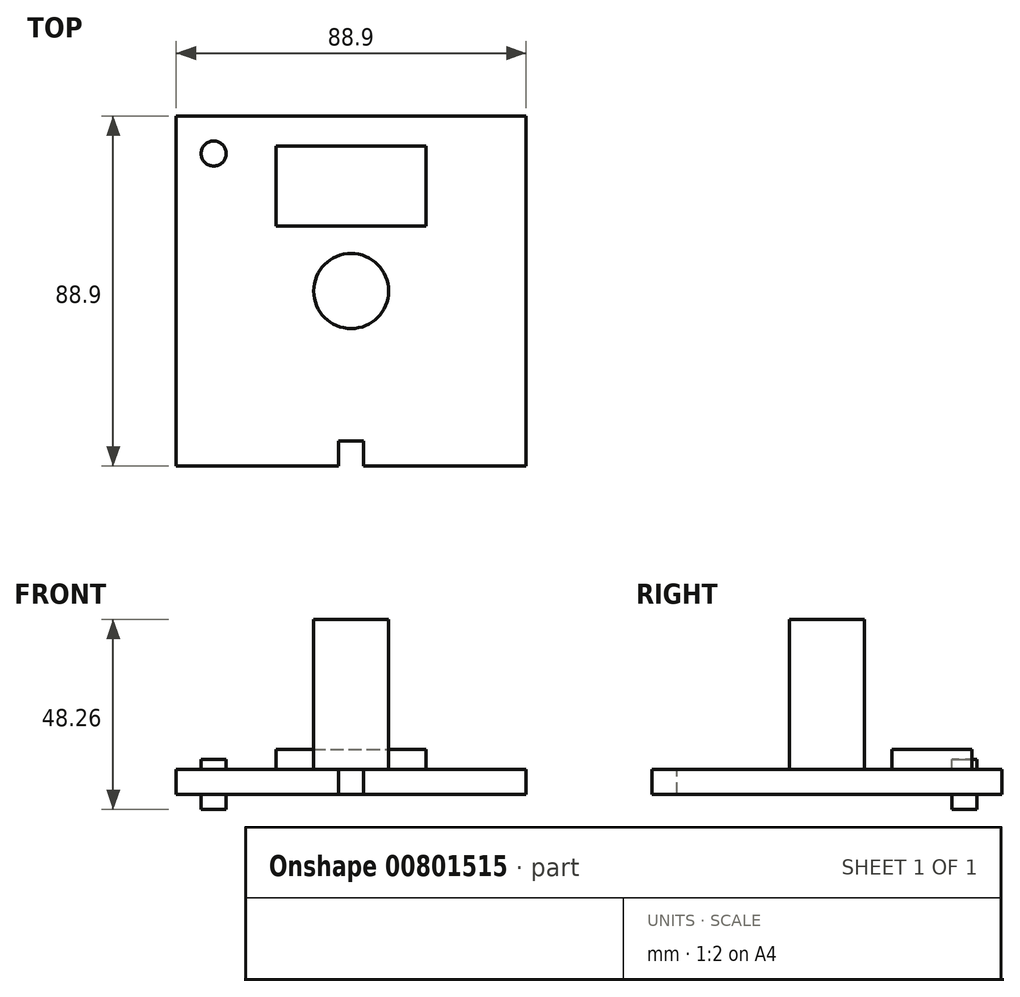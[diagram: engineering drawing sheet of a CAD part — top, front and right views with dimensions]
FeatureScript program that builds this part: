
annotation { "Feature Type Name" : "Feature", "Feature Type Description" : "" }
export const myFeature = defineFeature(function(context is Context, id is Id, definition is map)
    precondition{}
    {
        {
            var Q0;
            Q0=qCreatedBy(makeId("Top.planeOp"),FACE);
            var sketch = newSketch(context, id + "F0", { "sketchPlane" : qUnion([Q0])});
            skLineSegment(sketch, "E0.bottom", {"start": v(-44.45, 44.45) * mm, "end": v(44.45, 44.45) * mm});
            skLineSegment(sketch, "E0.top", {"start": v(-44.45, -44.45) * mm, "end": v(44.45, -44.45) * mm});
            skLineSegment(sketch, "E0.left", {"start": v(-44.45, 44.45) * mm, "end": v(-44.45, -44.45) * mm});
            skLineSegment(sketch, "E0.right", {"start": v(44.45, 44.45) * mm, "end": v(44.45, -44.45) * mm});
            skSolve(sketch);
        }
        {
            var Q0;
            Q0 = qSketchRegion(id + "F0", true);
            extrude(context, id + "F1", {"entities" : qUnion([Q0]), "depth" : 6.35 * mm, "offsetDistance" : 25.4 * mm});
        }
        {
            var Q0;
            Q0=makeQuery(id+"F1.opExtrude","CAP_FACE",FACE,{"disambiguationData":[OSD([sQuery(id+"F0.wireOp",EDGE,"E0.bottom"),sQuery(id+"F0.wireOp",EDGE,"E0.top"),sQuery(id+"F0.wireOp",EDGE,"E0.left"),sQuery(id+"F0.wireOp",EDGE,"E0.right")])],"isStart":false});
            var sketch = newSketch(context, id + "F2", { "sketchPlane" : qUnion([Q0])});
            skCircle(sketch, "E1", {"center": v(0, 0) * mm, "radius": 9.53 * mm});
            skSolve(sketch);
        }
        {
            var Q0;
            Q0 = qSketchRegion(id + "F2", true);
            extrude(context, id + "F3", {"entities" : qUnion([Q0]), "operationType" : NewBodyOperationType.ADD, "depth" : 38.1 * mm, "offsetDistance" : 25.4 * mm});
        }
        {
            var Q0;
            Q0=makeQuery(id+"F1.opExtrude","CAP_FACE",FACE,{"disambiguationData":[OSD([sQuery(id+"F0.wireOp",EDGE,"E0.bottom"),sQuery(id+"F0.wireOp",EDGE,"E0.top"),sQuery(id+"F0.wireOp",EDGE,"E0.left"),sQuery(id+"F0.wireOp",EDGE,"E0.right")])],"isStart":false});
            var sketch = newSketch(context, id + "F4", { "sketchPlane" : qUnion([Q0])});
            skLineSegment(sketch, "E2.bottom", {"start": v(-19.05, 36.83) * mm, "end": v(19.05, 36.83) * mm});
            skLineSegment(sketch, "E2.top", {"start": v(-19.05, 16.5) * mm, "end": v(19.05, 16.5) * mm});
            skLineSegment(sketch, "E2.left", {"start": v(-19.05, 36.83) * mm, "end": v(-19.05, 16.5) * mm});
            skLineSegment(sketch, "E2.right", {"start": v(19.05, 36.83) * mm, "end": v(19.05, 16.5) * mm});
            skLineSegment(sketch, "E3", {"start": v(0, 36.83) * mm, "end": v(0, 16.5) * mm, "construction": true});
            skSolve(sketch);
        }
        {
            var Q0;
            Q0 = qSketchRegion(id + "F4", true);
            extrude(context, id + "F5", {"entities" : qUnion([Q0]), "operationType" : NewBodyOperationType.ADD, "depth" : 5.08 * mm, "offsetDistance" : 25.4 * mm});
        }
        {
            var Q0;
            Q0=makeQuery(id+"F1.opExtrude","CAP_FACE",FACE,{"disambiguationData":[OSD([sQuery(id+"F0.wireOp",EDGE,"E0.bottom"),sQuery(id+"F0.wireOp",EDGE,"E0.top"),sQuery(id+"F0.wireOp",EDGE,"E0.left"),sQuery(id+"F0.wireOp",EDGE,"E0.right")])],"isStart":false});
            var sketch = newSketch(context, id + "F6", { "sketchPlane" : qUnion([Q0])});
            skCircle(sketch, "E4", {"center": v(-34.93, 34.92) * mm, "radius": 3.18 * mm});
            skSolve(sketch);
        }
        {
            var Q0;
            Q0 = qSketchRegion(id + "F6", true);
            extrude(context, id + "F7", {"entities" : qUnion([Q0]), "operationType" : NewBodyOperationType.ADD, "oppositeDirection" : true, "depth" : 10.16 * mm, "offsetDistance" : 25.4 * mm, "hasSecondDirection" : true, "secondDirectionOppositeDirection" : false, "secondDirectionDepth" : 2.54 * mm});
        }
        {
            var Q0;
            Q0=makeQuery(id+"F1.opExtrude","CAP_FACE",FACE,{"disambiguationData":[OSD([sQuery(id+"F0.wireOp",EDGE,"E0.bottom"),sQuery(id+"F0.wireOp",EDGE,"E0.top"),sQuery(id+"F0.wireOp",EDGE,"E0.left"),sQuery(id+"F0.wireOp",EDGE,"E0.right")])],"isStart":false});
            var sketch = newSketch(context, id + "F8", { "sketchPlane" : qUnion([Q0])});
            skLineSegment(sketch, "E5.bottom", {"start": v(3.18, -44.45) * mm, "end": v(-3.17, -44.45) * mm});
            skLineSegment(sketch, "E5.top", {"start": v(3.18, -38.1) * mm, "end": v(-3.17, -38.1) * mm});
            skLineSegment(sketch, "E5.left", {"start": v(3.18, -44.45) * mm, "end": v(3.18, -38.1) * mm});
            skLineSegment(sketch, "E5.right", {"start": v(-3.17, -44.45) * mm, "end": v(-3.17, -38.1) * mm});
            skLineSegment(sketch, "E6", {"start": v(-44.45, -44.45) * mm, "end": v(-3.17, -44.45) * mm, "construction": true});
            skLineSegment(sketch, "E7", {"start": v(3.18, -44.45) * mm, "end": v(44.45, -44.45) * mm, "construction": true});
            skSolve(sketch);
        }
        {
            var Q0;
            Q0 = qSketchRegion(id + "F8", true);
            extrude(context, id + "F9", {"entities" : qUnion([Q0]), "operationType" : NewBodyOperationType.REMOVE, "oppositeDirection" : true, "depth" : 6.35 * mm, "offsetDistance" : 25.4 * mm});
        }
    });
